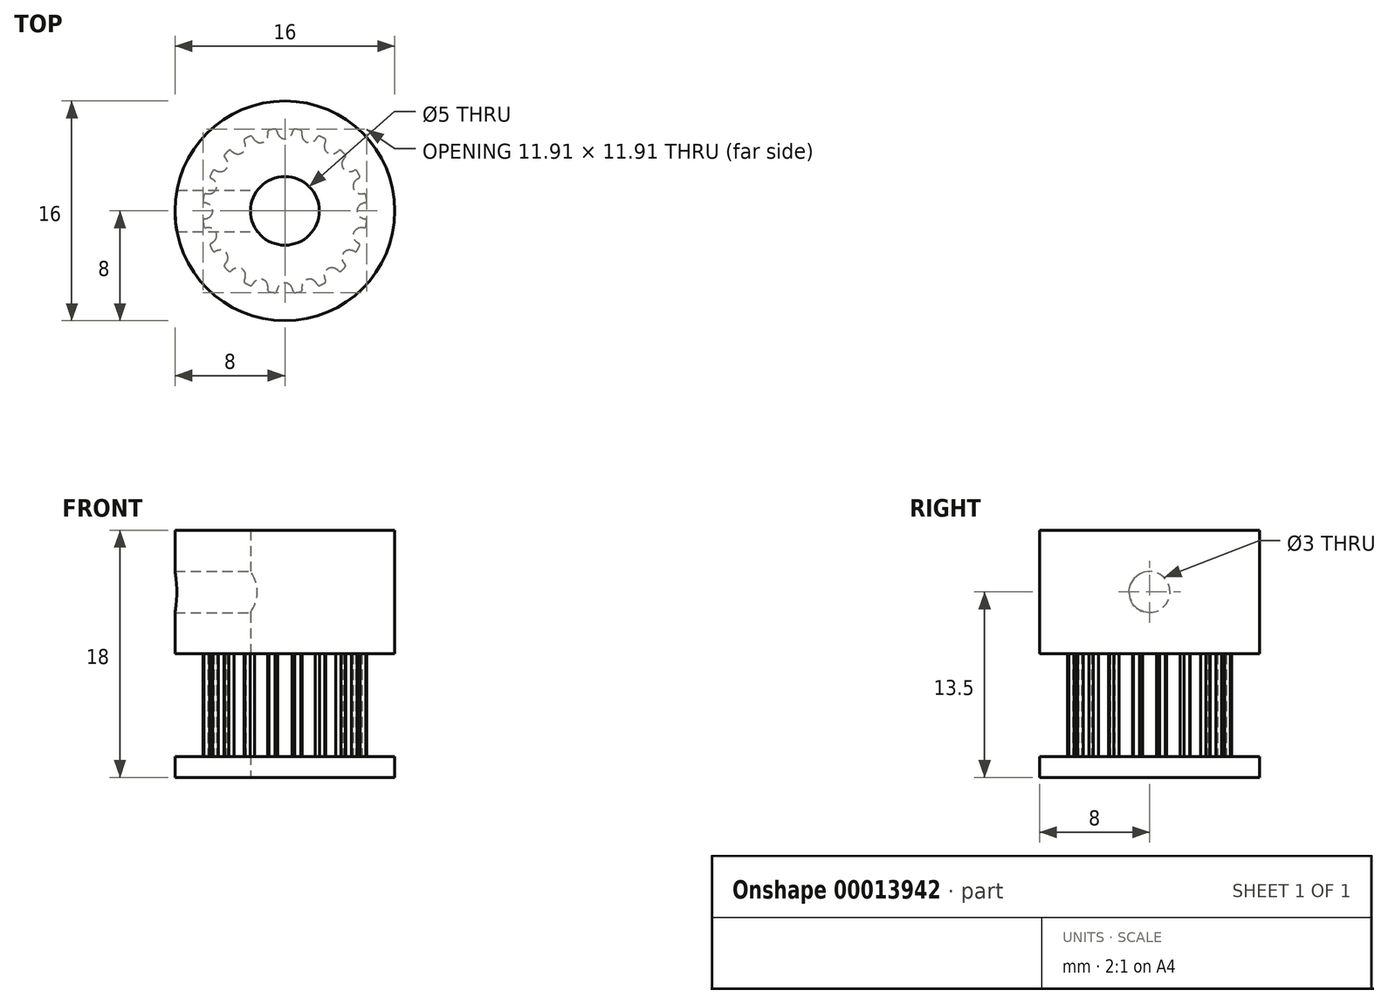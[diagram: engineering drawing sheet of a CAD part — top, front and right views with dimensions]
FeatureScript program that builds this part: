
annotation { "Feature Type Name" : "Feature", "Feature Type Description" : "" }
export const myFeature = defineFeature(function(context is Context, id is Id, definition is map)
    precondition{}
    {
        {
            var Q0;
            Q0=qCreatedBy(makeId("Top.planeOp"),FACE);
            var sketch = newSketch(context, id + "F0", { "sketchPlane" : qUnion([Q0])});
            skLineSegment(sketch, "E0", {"start": v(-19.17, 17.78) * mm, "end": v(-18.17, 17.78) * mm});
            skLineSegment(sketch, "E1", {"start": v(-18.17, 17.78) * mm, "end": v(-18.17, 18.4) * mm});
            skArc(sketch, "E2", {"start": v(-18.67, 18.85) * mm, "mid": v(-18.88, 19.07) * mm, "end": v(-19.17, 19.16) * mm});
            skArc(sketch, "E3", {"start": v(-18.58, 18.54) * mm, "mid": v(-18.61, 18.7) * mm, "end": v(-18.67, 18.85) * mm});
            skArc(sketch, "E4", {"start": v(-18.58, 18.54) * mm, "mid": v(-18.53, 18.44) * mm, "end": v(-18.43, 18.4) * mm});
            skLineSegment(sketch, "E5", {"start": v(-18.43, 18.4) * mm, "end": v(-18.17, 18.4) * mm});
            skArc(sketch, "E6.0.MirrorCS", {"start": v(-19.67, 18.85) * mm, "mid": v(-19.47, 19.07) * mm, "end": v(-19.17, 19.16) * mm});
            skArc(sketch, "E7.0.MirrorCS", {"start": v(-19.76, 18.54) * mm, "mid": v(-19.73, 18.7) * mm, "end": v(-19.67, 18.85) * mm});
            skArc(sketch, "E8.0.MirrorCS", {"start": v(-19.76, 18.54) * mm, "mid": v(-19.81, 18.44) * mm, "end": v(-19.91, 18.4) * mm});
            skLineSegment(sketch, "E9.0.MirrorCS", {"start": v(-19.91, 18.4) * mm, "end": v(-20.17, 18.4) * mm});
            skLineSegment(sketch, "E10.0.MirrorCS", {"start": v(-20.17, 17.78) * mm, "end": v(-20.17, 18.4) * mm});
            skLineSegment(sketch, "E11.0.MirrorCS", {"start": v(-19.17, 17.78) * mm, "end": v(-20.17, 17.78) * mm});
            skLineSegment(sketch, "E12.direction1", {"start": v(-20.17, 17.78) * mm, "end": v(-18.17, 17.78) * mm, "construction": true});
            skLineSegment(sketch, "E13", {"start": v(-20.17, 18.15) * mm, "end": v(-18.17, 18.15) * mm, "construction": true});
            skPoint(sketch, "E14", {"position": v(0, -5.25) * mm});
            skArc(sketch, "E15", {"start": v(0.51, -5.6) * mm, "mid": v(0, -5.25) * mm, "end": v(-0.51, -5.6) * mm});
            skArc(sketch, "E16", {"start": v(-0.51, -5.6) * mm, "mid": v(-0.56, -5.71) * mm, "end": v(-0.59, -5.83) * mm});
            skArc(sketch, "E17", {"start": v(0.59, -5.83) * mm, "mid": v(0.56, -5.71) * mm, "end": v(0.51, -5.6) * mm});
            skArc(sketch, "E18", {"start": v(0.72, -5.96) * mm, "mid": v(0.94, -5.93) * mm, "end": v(1.16, -5.89) * mm});
            skArc(sketch, "E19", {"start": v(0.59, -5.83) * mm, "mid": v(0.66, -5.94) * mm, "end": v(0.8, -5.95) * mm});
            skArc(sketch, "E20", {"start": v(-0.59, -5.83) * mm, "mid": v(-0.66, -5.94) * mm, "end": v(-0.8, -5.95) * mm});
            skArc(sketch, "E21.1.0", {"start": v(2.22, -5.16) * mm, "mid": v(1.62, -5) * mm, "end": v(1.24, -5.48) * mm});
            skPoint(sketch, "E21.1.1", {"position": v(1.62, -5) * mm});
            skArc(sketch, "E21.1.2", {"start": v(1.24, -5.48) * mm, "mid": v(1.23, -5.6) * mm, "end": v(1.24, -5.73) * mm});
            skArc(sketch, "E21.1.3", {"start": v(2.36, -5.37) * mm, "mid": v(2.47, -5.44) * mm, "end": v(2.6, -5.41) * mm});
            skArc(sketch, "E21.1.4", {"start": v(1.24, -5.73) * mm, "mid": v(1.2, -5.85) * mm, "end": v(1.08, -5.9) * mm});
            skArc(sketch, "E21.1.5", {"start": v(2.36, -5.37) * mm, "mid": v(2.3, -5.26) * mm, "end": v(2.22, -5.16) * mm});
            skArc(sketch, "E22.3.2.0", {"start": v(3.7, -4.22) * mm, "mid": v(3.09, -4.25) * mm, "end": v(2.87, -4.83) * mm});
            skPoint(sketch, "E22.4.2.0", {"position": v(3.09, -4.25) * mm});
            skArc(sketch, "E22.5.2.0", {"start": v(2.87, -4.83) * mm, "mid": v(2.9, -4.95) * mm, "end": v(2.95, -5.07) * mm});
            skArc(sketch, "E22.9.2.0", {"start": v(3.9, -4.37) * mm, "mid": v(4.03, -4.41) * mm, "end": v(4.14, -4.35) * mm});
            skArc(sketch, "E22.13.2.0", {"start": v(2.95, -5.07) * mm, "mid": v(2.95, -5.2) * mm, "end": v(2.85, -5.28) * mm});
            skArc(sketch, "E22.17.2.0", {"start": v(3.9, -4.37) * mm, "mid": v(3.81, -4.3) * mm, "end": v(3.7, -4.22) * mm});
            skArc(sketch, "E22.3.3.0", {"start": v(4.83, -2.87) * mm, "mid": v(4.25, -3.09) * mm, "end": v(4.22, -3.7) * mm});
            skPoint(sketch, "E22.4.3.0", {"position": v(4.25, -3.09) * mm});
            skArc(sketch, "E22.5.3.0", {"start": v(4.22, -3.7) * mm, "mid": v(4.3, -3.81) * mm, "end": v(4.37, -3.9) * mm});
            skArc(sketch, "E22.9.3.0", {"start": v(5.07, -2.95) * mm, "mid": v(5.2, -2.95) * mm, "end": v(5.28, -2.85) * mm});
            skArc(sketch, "E22.13.3.0", {"start": v(4.37, -3.9) * mm, "mid": v(4.41, -4.03) * mm, "end": v(4.35, -4.14) * mm});
            skArc(sketch, "E22.17.3.0", {"start": v(5.07, -2.95) * mm, "mid": v(4.95, -2.9) * mm, "end": v(4.83, -2.87) * mm});
            skArc(sketch, "E22.3.4.0", {"start": v(5.48, -1.24) * mm, "mid": v(5, -1.62) * mm, "end": v(5.16, -2.22) * mm});
            skPoint(sketch, "E22.4.4.0", {"position": v(5, -1.62) * mm});
            skArc(sketch, "E22.5.4.0", {"start": v(5.16, -2.22) * mm, "mid": v(5.26, -2.3) * mm, "end": v(5.37, -2.36) * mm});
            skArc(sketch, "E22.9.4.0", {"start": v(5.73, -1.24) * mm, "mid": v(5.85, -1.2) * mm, "end": v(5.9, -1.08) * mm});
            skArc(sketch, "E22.13.4.0", {"start": v(5.37, -2.36) * mm, "mid": v(5.44, -2.47) * mm, "end": v(5.41, -2.6) * mm});
            skArc(sketch, "E22.17.4.0", {"start": v(5.73, -1.24) * mm, "mid": v(5.6, -1.23) * mm, "end": v(5.48, -1.24) * mm});
            skArc(sketch, "E22.3.5.0", {"start": v(5.6, 0.51) * mm, "mid": v(5.25, 0) * mm, "end": v(5.6, -0.51) * mm});
            skPoint(sketch, "E22.4.5.0", {"position": v(5.25, 0) * mm});
            skArc(sketch, "E22.5.5.0", {"start": v(5.6, -0.51) * mm, "mid": v(5.71, -0.56) * mm, "end": v(5.83, -0.59) * mm});
            skArc(sketch, "E22.9.5.0", {"start": v(5.83, 0.59) * mm, "mid": v(5.94, 0.66) * mm, "end": v(5.95, 0.8) * mm});
            skArc(sketch, "E22.13.5.0", {"start": v(5.83, -0.59) * mm, "mid": v(5.94, -0.66) * mm, "end": v(5.95, -0.8) * mm});
            skArc(sketch, "E22.17.5.0", {"start": v(5.83, 0.59) * mm, "mid": v(5.71, 0.56) * mm, "end": v(5.6, 0.51) * mm});
            skArc(sketch, "E22.3.6.0", {"start": v(5.16, 2.22) * mm, "mid": v(5, 1.62) * mm, "end": v(5.48, 1.24) * mm});
            skPoint(sketch, "E22.4.6.0", {"position": v(5, 1.62) * mm});
            skArc(sketch, "E22.5.6.0", {"start": v(5.48, 1.24) * mm, "mid": v(5.6, 1.23) * mm, "end": v(5.73, 1.24) * mm});
            skArc(sketch, "E22.9.6.0", {"start": v(5.37, 2.36) * mm, "mid": v(5.44, 2.47) * mm, "end": v(5.41, 2.6) * mm});
            skArc(sketch, "E22.13.6.0", {"start": v(5.73, 1.24) * mm, "mid": v(5.85, 1.2) * mm, "end": v(5.9, 1.08) * mm});
            skArc(sketch, "E22.17.6.0", {"start": v(5.37, 2.36) * mm, "mid": v(5.26, 2.3) * mm, "end": v(5.16, 2.22) * mm});
            skArc(sketch, "E22.3.7.0", {"start": v(4.22, 3.7) * mm, "mid": v(4.25, 3.09) * mm, "end": v(4.83, 2.87) * mm});
            skPoint(sketch, "E22.4.7.0", {"position": v(4.25, 3.09) * mm});
            skArc(sketch, "E22.5.7.0", {"start": v(4.83, 2.87) * mm, "mid": v(4.95, 2.9) * mm, "end": v(5.07, 2.95) * mm});
            skArc(sketch, "E22.9.7.0", {"start": v(4.37, 3.9) * mm, "mid": v(4.41, 4.03) * mm, "end": v(4.35, 4.14) * mm});
            skArc(sketch, "E22.13.7.0", {"start": v(5.07, 2.95) * mm, "mid": v(5.2, 2.95) * mm, "end": v(5.28, 2.85) * mm});
            skArc(sketch, "E22.17.7.0", {"start": v(4.37, 3.9) * mm, "mid": v(4.3, 3.81) * mm, "end": v(4.22, 3.7) * mm});
            skArc(sketch, "E22.3.8.0", {"start": v(2.87, 4.83) * mm, "mid": v(3.09, 4.25) * mm, "end": v(3.7, 4.22) * mm});
            skPoint(sketch, "E22.4.8.0", {"position": v(3.09, 4.25) * mm});
            skArc(sketch, "E22.5.8.0", {"start": v(3.7, 4.22) * mm, "mid": v(3.81, 4.3) * mm, "end": v(3.9, 4.37) * mm});
            skArc(sketch, "E22.9.8.0", {"start": v(2.95, 5.07) * mm, "mid": v(2.95, 5.2) * mm, "end": v(2.85, 5.28) * mm});
            skArc(sketch, "E22.13.8.0", {"start": v(3.9, 4.37) * mm, "mid": v(4.03, 4.41) * mm, "end": v(4.14, 4.35) * mm});
            skArc(sketch, "E22.17.8.0", {"start": v(2.95, 5.07) * mm, "mid": v(2.9, 4.95) * mm, "end": v(2.87, 4.83) * mm});
            skArc(sketch, "E22.3.9.0", {"start": v(1.24, 5.48) * mm, "mid": v(1.62, 5) * mm, "end": v(2.22, 5.16) * mm});
            skPoint(sketch, "E22.4.9.0", {"position": v(1.62, 5) * mm});
            skArc(sketch, "E22.5.9.0", {"start": v(2.22, 5.16) * mm, "mid": v(2.3, 5.26) * mm, "end": v(2.36, 5.37) * mm});
            skArc(sketch, "E22.9.9.0", {"start": v(1.24, 5.73) * mm, "mid": v(1.2, 5.85) * mm, "end": v(1.08, 5.9) * mm});
            skArc(sketch, "E22.13.9.0", {"start": v(2.36, 5.37) * mm, "mid": v(2.47, 5.44) * mm, "end": v(2.6, 5.41) * mm});
            skArc(sketch, "E22.17.9.0", {"start": v(1.24, 5.73) * mm, "mid": v(1.23, 5.6) * mm, "end": v(1.24, 5.48) * mm});
            skArc(sketch, "E22.3.10.0", {"start": v(-0.51, 5.6) * mm, "mid": v(0, 5.25) * mm, "end": v(0.51, 5.6) * mm});
            skPoint(sketch, "E22.4.10.0", {"position": v(0, 5.25) * mm});
            skArc(sketch, "E22.5.10.0", {"start": v(0.51, 5.6) * mm, "mid": v(0.56, 5.71) * mm, "end": v(0.59, 5.83) * mm});
            skArc(sketch, "E22.9.10.0", {"start": v(-0.59, 5.83) * mm, "mid": v(-0.66, 5.94) * mm, "end": v(-0.8, 5.95) * mm});
            skArc(sketch, "E22.13.10.0", {"start": v(0.59, 5.83) * mm, "mid": v(0.66, 5.94) * mm, "end": v(0.8, 5.95) * mm});
            skArc(sketch, "E22.17.10.0", {"start": v(-0.59, 5.83) * mm, "mid": v(-0.56, 5.71) * mm, "end": v(-0.51, 5.6) * mm});
            skArc(sketch, "E22.3.11.0", {"start": v(-2.22, 5.16) * mm, "mid": v(-1.62, 5) * mm, "end": v(-1.24, 5.48) * mm});
            skPoint(sketch, "E22.4.11.0", {"position": v(-1.62, 5) * mm});
            skArc(sketch, "E22.5.11.0", {"start": v(-1.24, 5.48) * mm, "mid": v(-1.23, 5.6) * mm, "end": v(-1.24, 5.73) * mm});
            skArc(sketch, "E22.9.11.0", {"start": v(-2.36, 5.37) * mm, "mid": v(-2.47, 5.44) * mm, "end": v(-2.6, 5.41) * mm});
            skArc(sketch, "E22.13.11.0", {"start": v(-1.24, 5.73) * mm, "mid": v(-1.2, 5.85) * mm, "end": v(-1.08, 5.9) * mm});
            skArc(sketch, "E22.17.11.0", {"start": v(-2.36, 5.37) * mm, "mid": v(-2.3, 5.26) * mm, "end": v(-2.22, 5.16) * mm});
            skArc(sketch, "E22.3.12.0", {"start": v(-3.7, 4.22) * mm, "mid": v(-3.09, 4.25) * mm, "end": v(-2.87, 4.83) * mm});
            skPoint(sketch, "E22.4.12.0", {"position": v(-3.09, 4.25) * mm});
            skArc(sketch, "E22.5.12.0", {"start": v(-2.87, 4.83) * mm, "mid": v(-2.9, 4.95) * mm, "end": v(-2.95, 5.07) * mm});
            skArc(sketch, "E22.9.12.0", {"start": v(-3.9, 4.37) * mm, "mid": v(-4.03, 4.41) * mm, "end": v(-4.14, 4.35) * mm});
            skArc(sketch, "E22.13.12.0", {"start": v(-2.95, 5.07) * mm, "mid": v(-2.95, 5.2) * mm, "end": v(-2.85, 5.28) * mm});
            skArc(sketch, "E22.17.12.0", {"start": v(-3.9, 4.37) * mm, "mid": v(-3.81, 4.3) * mm, "end": v(-3.7, 4.22) * mm});
            skArc(sketch, "E22.3.13.0", {"start": v(-4.83, 2.87) * mm, "mid": v(-4.25, 3.09) * mm, "end": v(-4.22, 3.7) * mm});
            skPoint(sketch, "E22.4.13.0", {"position": v(-4.25, 3.09) * mm});
            skArc(sketch, "E22.5.13.0", {"start": v(-4.22, 3.7) * mm, "mid": v(-4.3, 3.81) * mm, "end": v(-4.37, 3.9) * mm});
            skArc(sketch, "E22.9.13.0", {"start": v(-5.07, 2.95) * mm, "mid": v(-5.2, 2.95) * mm, "end": v(-5.28, 2.85) * mm});
            skArc(sketch, "E22.13.13.0", {"start": v(-4.37, 3.9) * mm, "mid": v(-4.41, 4.03) * mm, "end": v(-4.35, 4.14) * mm});
            skArc(sketch, "E22.17.13.0", {"start": v(-5.07, 2.95) * mm, "mid": v(-4.95, 2.9) * mm, "end": v(-4.83, 2.87) * mm});
            skArc(sketch, "E22.3.14.0", {"start": v(-5.48, 1.24) * mm, "mid": v(-5, 1.62) * mm, "end": v(-5.16, 2.22) * mm});
            skPoint(sketch, "E22.4.14.0", {"position": v(-5, 1.62) * mm});
            skArc(sketch, "E22.5.14.0", {"start": v(-5.16, 2.22) * mm, "mid": v(-5.26, 2.3) * mm, "end": v(-5.37, 2.36) * mm});
            skArc(sketch, "E22.9.14.0", {"start": v(-5.73, 1.24) * mm, "mid": v(-5.85, 1.2) * mm, "end": v(-5.9, 1.08) * mm});
            skArc(sketch, "E22.13.14.0", {"start": v(-5.37, 2.36) * mm, "mid": v(-5.44, 2.47) * mm, "end": v(-5.41, 2.6) * mm});
            skArc(sketch, "E22.17.14.0", {"start": v(-5.73, 1.24) * mm, "mid": v(-5.6, 1.23) * mm, "end": v(-5.48, 1.24) * mm});
            skArc(sketch, "E22.3.15.0", {"start": v(-5.6, -0.51) * mm, "mid": v(-5.25, 0) * mm, "end": v(-5.6, 0.51) * mm});
            skPoint(sketch, "E22.4.15.0", {"position": v(-5.25, 0) * mm});
            skArc(sketch, "E22.5.15.0", {"start": v(-5.6, 0.51) * mm, "mid": v(-5.71, 0.56) * mm, "end": v(-5.83, 0.59) * mm});
            skArc(sketch, "E22.9.15.0", {"start": v(-5.83, -0.59) * mm, "mid": v(-5.94, -0.66) * mm, "end": v(-5.95, -0.8) * mm});
            skArc(sketch, "E22.13.15.0", {"start": v(-5.83, 0.59) * mm, "mid": v(-5.94, 0.66) * mm, "end": v(-5.95, 0.8) * mm});
            skArc(sketch, "E22.17.15.0", {"start": v(-5.83, -0.59) * mm, "mid": v(-5.71, -0.56) * mm, "end": v(-5.6, -0.51) * mm});
            skArc(sketch, "E22.3.16.0", {"start": v(-5.16, -2.22) * mm, "mid": v(-5, -1.62) * mm, "end": v(-5.48, -1.24) * mm});
            skPoint(sketch, "E22.4.16.0", {"position": v(-5, -1.62) * mm});
            skArc(sketch, "E22.5.16.0", {"start": v(-5.48, -1.24) * mm, "mid": v(-5.6, -1.23) * mm, "end": v(-5.73, -1.24) * mm});
            skArc(sketch, "E22.9.16.0", {"start": v(-5.37, -2.36) * mm, "mid": v(-5.44, -2.47) * mm, "end": v(-5.41, -2.6) * mm});
            skArc(sketch, "E22.13.16.0", {"start": v(-5.73, -1.24) * mm, "mid": v(-5.85, -1.2) * mm, "end": v(-5.9, -1.08) * mm});
            skArc(sketch, "E22.17.16.0", {"start": v(-5.37, -2.36) * mm, "mid": v(-5.26, -2.3) * mm, "end": v(-5.16, -2.22) * mm});
            skArc(sketch, "E22.3.17.0", {"start": v(-4.22, -3.7) * mm, "mid": v(-4.25, -3.09) * mm, "end": v(-4.83, -2.87) * mm});
            skPoint(sketch, "E22.4.17.0", {"position": v(-4.25, -3.09) * mm});
            skArc(sketch, "E22.5.17.0", {"start": v(-4.83, -2.87) * mm, "mid": v(-4.95, -2.9) * mm, "end": v(-5.07, -2.95) * mm});
            skArc(sketch, "E22.9.17.0", {"start": v(-4.37, -3.9) * mm, "mid": v(-4.41, -4.03) * mm, "end": v(-4.35, -4.14) * mm});
            skArc(sketch, "E22.13.17.0", {"start": v(-5.07, -2.95) * mm, "mid": v(-5.2, -2.95) * mm, "end": v(-5.28, -2.85) * mm});
            skArc(sketch, "E22.17.17.0", {"start": v(-4.37, -3.9) * mm, "mid": v(-4.3, -3.81) * mm, "end": v(-4.22, -3.7) * mm});
            skArc(sketch, "E22.3.18.0", {"start": v(-2.87, -4.83) * mm, "mid": v(-3.09, -4.25) * mm, "end": v(-3.7, -4.22) * mm});
            skPoint(sketch, "E22.4.18.0", {"position": v(-3.09, -4.25) * mm});
            skArc(sketch, "E22.5.18.0", {"start": v(-3.7, -4.22) * mm, "mid": v(-3.81, -4.3) * mm, "end": v(-3.9, -4.37) * mm});
            skArc(sketch, "E22.9.18.0", {"start": v(-2.95, -5.07) * mm, "mid": v(-2.95, -5.2) * mm, "end": v(-2.85, -5.28) * mm});
            skArc(sketch, "E22.13.18.0", {"start": v(-3.9, -4.37) * mm, "mid": v(-4.03, -4.41) * mm, "end": v(-4.14, -4.35) * mm});
            skArc(sketch, "E22.17.18.0", {"start": v(-2.95, -5.07) * mm, "mid": v(-2.9, -4.95) * mm, "end": v(-2.87, -4.83) * mm});
            skArc(sketch, "E22.3.19.0", {"start": v(-1.24, -5.48) * mm, "mid": v(-1.62, -5) * mm, "end": v(-2.22, -5.16) * mm});
            skPoint(sketch, "E22.4.19.0", {"position": v(-1.62, -5) * mm});
            skArc(sketch, "E22.5.19.0", {"start": v(-2.22, -5.16) * mm, "mid": v(-2.3, -5.26) * mm, "end": v(-2.36, -5.37) * mm});
            skArc(sketch, "E22.9.19.0", {"start": v(-1.24, -5.73) * mm, "mid": v(-1.2, -5.85) * mm, "end": v(-1.08, -5.9) * mm});
            skArc(sketch, "E22.13.19.0", {"start": v(-2.36, -5.37) * mm, "mid": v(-2.47, -5.44) * mm, "end": v(-2.6, -5.41) * mm});
            skArc(sketch, "E22.17.19.0", {"start": v(-1.24, -5.73) * mm, "mid": v(-1.23, -5.6) * mm, "end": v(-1.24, -5.48) * mm});
            skArc(sketch, "E23.trimOffspring", {"start": v(2.52, -5.44) * mm, "mid": v(2.72, -5.35) * mm, "end": v(2.92, -5.24) * mm});
            skArc(sketch, "E24.trimOffspring", {"start": v(4.08, -4.4) * mm, "mid": v(4.24, -4.24) * mm, "end": v(4.4, -4.08) * mm});
            skArc(sketch, "E25.trimOffspring", {"start": v(5.24, -2.92) * mm, "mid": v(5.33, -2.76) * mm, "end": v(5.41, -2.6) * mm});
            skArc(sketch, "E26.trimOffspring", {"start": v(5.89, -1.16) * mm, "mid": v(5.93, -0.94) * mm, "end": v(5.96, -0.72) * mm});
            skArc(sketch, "E27.trimOffspring", {"start": v(5.44, 2.52) * mm, "mid": v(5.35, 2.72) * mm, "end": v(5.24, 2.92) * mm});
            skArc(sketch, "E28.trimOffspring", {"start": v(4.4, 4.08) * mm, "mid": v(4.24, 4.24) * mm, "end": v(4.08, 4.4) * mm});
            skArc(sketch, "E29.trimOffspring", {"start": v(5.96, 0.72) * mm, "mid": v(5.93, 0.94) * mm, "end": v(5.89, 1.16) * mm});
            skArc(sketch, "E30.trimOffspring", {"start": v(2.92, 5.24) * mm, "mid": v(2.72, 5.35) * mm, "end": v(2.52, 5.44) * mm});
            skArc(sketch, "E31.trimOffspring", {"start": v(1.16, 5.89) * mm, "mid": v(0.94, 5.93) * mm, "end": v(0.72, 5.96) * mm});
            skArc(sketch, "E32.trimOffspring", {"start": v(-0.72, 5.96) * mm, "mid": v(-0.94, 5.93) * mm, "end": v(-1.16, 5.89) * mm});
            skArc(sketch, "E33.trimOffspring", {"start": v(-2.52, 5.44) * mm, "mid": v(-2.72, 5.35) * mm, "end": v(-2.92, 5.24) * mm});
            skArc(sketch, "E34.trimOffspring", {"start": v(-4.08, 4.4) * mm, "mid": v(-4.24, 4.24) * mm, "end": v(-4.4, 4.08) * mm});
            skArc(sketch, "E35.trimOffspring", {"start": v(-5.24, 2.92) * mm, "mid": v(-5.35, 2.72) * mm, "end": v(-5.44, 2.52) * mm});
            skArc(sketch, "E36.trimOffspring", {"start": v(-5.89, 1.16) * mm, "mid": v(-5.93, 0.94) * mm, "end": v(-5.96, 0.72) * mm});
            skArc(sketch, "E37.trimOffspring", {"start": v(-5.96, -0.72) * mm, "mid": v(-5.93, -0.94) * mm, "end": v(-5.89, -1.16) * mm});
            skArc(sketch, "E38.trimOffspring", {"start": v(-5.44, -2.52) * mm, "mid": v(-5.35, -2.72) * mm, "end": v(-5.24, -2.92) * mm});
            skArc(sketch, "E39.trimOffspring", {"start": v(-4.4, -4.08) * mm, "mid": v(-4.24, -4.24) * mm, "end": v(-4.08, -4.4) * mm});
            skArc(sketch, "E40.trimOffspring", {"start": v(-2.92, -5.24) * mm, "mid": v(-2.72, -5.35) * mm, "end": v(-2.52, -5.44) * mm});
            skArc(sketch, "E41.trimOffspring", {"start": v(-1.16, -5.89) * mm, "mid": v(-0.94, -5.93) * mm, "end": v(-0.72, -5.96) * mm});
            skSolve(sketch);
        }
        {
            var Q0;
            Q0=makeQuery(id+"F0.imprint","IMPRINT",FACE,{"disambiguationData":[TD([[makeQuery(id+"F0.imprint","IMPRINT",EDGE,{"derivedFrom":sQuery(id+"F0.wireOp",EDGE,"E15")}),-1.0]])]});
            extrude(context, id + "F1", {"entities" : qUnion([Q0]), "depth" : 7.5 * mm});
        }
        {
            var Q0;
            Q0=makeQuery(id+"F1.opExtrude","CAP_FACE",FACE,{"disambiguationData":[OSD([sQuery(id+"F0.wireOp",EDGE,"E15"),sQuery(id+"F0.wireOp",EDGE,"E16"),sQuery(id+"F0.wireOp",EDGE,"E17"),sQuery(id+"F0.wireOp",EDGE,"E18"),sQuery(id+"F0.wireOp",EDGE,"E19"),sQuery(id+"F0.wireOp",EDGE,"E20"),sQuery(id+"F0.wireOp",EDGE,"E21.1.0"),sQuery(id+"F0.wireOp",EDGE,"E21.1.2"),sQuery(id+"F0.wireOp",EDGE,"E21.1.3"),sQuery(id+"F0.wireOp",EDGE,"E21.1.4"),sQuery(id+"F0.wireOp",EDGE,"E21.1.5"),sQuery(id+"F0.wireOp",EDGE,"E22.3.2.0"),sQuery(id+"F0.wireOp",EDGE,"E22.5.2.0"),sQuery(id+"F0.wireOp",EDGE,"E22.9.2.0"),sQuery(id+"F0.wireOp",EDGE,"E22.13.2.0"),sQuery(id+"F0.wireOp",EDGE,"E22.17.2.0"),sQuery(id+"F0.wireOp",EDGE,"E22.3.3.0"),sQuery(id+"F0.wireOp",EDGE,"E22.5.3.0"),sQuery(id+"F0.wireOp",EDGE,"E22.9.3.0"),sQuery(id+"F0.wireOp",EDGE,"E22.13.3.0"),sQuery(id+"F0.wireOp",EDGE,"E22.17.3.0"),sQuery(id+"F0.wireOp",EDGE,"E22.3.4.0"),sQuery(id+"F0.wireOp",EDGE,"E22.5.4.0"),sQuery(id+"F0.wireOp",EDGE,"E22.9.4.0"),sQuery(id+"F0.wireOp",EDGE,"E22.13.4.0"),sQuery(id+"F0.wireOp",EDGE,"E22.17.4.0"),sQuery(id+"F0.wireOp",EDGE,"E22.3.5.0"),sQuery(id+"F0.wireOp",EDGE,"E22.5.5.0"),sQuery(id+"F0.wireOp",EDGE,"E22.9.5.0"),sQuery(id+"F0.wireOp",EDGE,"E22.13.5.0"),sQuery(id+"F0.wireOp",EDGE,"E22.17.5.0"),sQuery(id+"F0.wireOp",EDGE,"E22.3.6.0"),sQuery(id+"F0.wireOp",EDGE,"E22.5.6.0"),sQuery(id+"F0.wireOp",EDGE,"E22.9.6.0"),sQuery(id+"F0.wireOp",EDGE,"E22.13.6.0"),sQuery(id+"F0.wireOp",EDGE,"E22.17.6.0"),sQuery(id+"F0.wireOp",EDGE,"E22.3.7.0"),sQuery(id+"F0.wireOp",EDGE,"E22.5.7.0"),sQuery(id+"F0.wireOp",EDGE,"E22.9.7.0"),sQuery(id+"F0.wireOp",EDGE,"E22.13.7.0"),sQuery(id+"F0.wireOp",EDGE,"E22.17.7.0"),sQuery(id+"F0.wireOp",EDGE,"E22.3.8.0"),sQuery(id+"F0.wireOp",EDGE,"E22.5.8.0"),sQuery(id+"F0.wireOp",EDGE,"E22.9.8.0"),sQuery(id+"F0.wireOp",EDGE,"E22.13.8.0"),sQuery(id+"F0.wireOp",EDGE,"E22.17.8.0"),sQuery(id+"F0.wireOp",EDGE,"E22.3.9.0"),sQuery(id+"F0.wireOp",EDGE,"E22.5.9.0"),sQuery(id+"F0.wireOp",EDGE,"E22.9.9.0"),sQuery(id+"F0.wireOp",EDGE,"E22.13.9.0"),sQuery(id+"F0.wireOp",EDGE,"E22.17.9.0"),sQuery(id+"F0.wireOp",EDGE,"E22.3.10.0"),sQuery(id+"F0.wireOp",EDGE,"E22.5.10.0"),sQuery(id+"F0.wireOp",EDGE,"E22.9.10.0"),sQuery(id+"F0.wireOp",EDGE,"E22.13.10.0"),sQuery(id+"F0.wireOp",EDGE,"E22.17.10.0"),sQuery(id+"F0.wireOp",EDGE,"E22.3.11.0"),sQuery(id+"F0.wireOp",EDGE,"E22.5.11.0"),sQuery(id+"F0.wireOp",EDGE,"E22.9.11.0"),sQuery(id+"F0.wireOp",EDGE,"E22.13.11.0"),sQuery(id+"F0.wireOp",EDGE,"E22.17.11.0"),sQuery(id+"F0.wireOp",EDGE,"E22.3.12.0"),sQuery(id+"F0.wireOp",EDGE,"E22.5.12.0"),sQuery(id+"F0.wireOp",EDGE,"E22.9.12.0"),sQuery(id+"F0.wireOp",EDGE,"E22.13.12.0"),sQuery(id+"F0.wireOp",EDGE,"E22.17.12.0"),sQuery(id+"F0.wireOp",EDGE,"E22.3.13.0"),sQuery(id+"F0.wireOp",EDGE,"E22.5.13.0"),sQuery(id+"F0.wireOp",EDGE,"E22.9.13.0"),sQuery(id+"F0.wireOp",EDGE,"E22.13.13.0"),sQuery(id+"F0.wireOp",EDGE,"E22.17.13.0"),sQuery(id+"F0.wireOp",EDGE,"E22.3.14.0"),sQuery(id+"F0.wireOp",EDGE,"E22.5.14.0"),sQuery(id+"F0.wireOp",EDGE,"E22.9.14.0"),sQuery(id+"F0.wireOp",EDGE,"E22.13.14.0"),sQuery(id+"F0.wireOp",EDGE,"E22.17.14.0"),sQuery(id+"F0.wireOp",EDGE,"E22.3.15.0"),sQuery(id+"F0.wireOp",EDGE,"E22.5.15.0"),sQuery(id+"F0.wireOp",EDGE,"E22.9.15.0"),sQuery(id+"F0.wireOp",EDGE,"E22.13.15.0"),sQuery(id+"F0.wireOp",EDGE,"E22.17.15.0"),sQuery(id+"F0.wireOp",EDGE,"E22.3.16.0"),sQuery(id+"F0.wireOp",EDGE,"E22.5.16.0"),sQuery(id+"F0.wireOp",EDGE,"E22.9.16.0"),sQuery(id+"F0.wireOp",EDGE,"E22.13.16.0"),sQuery(id+"F0.wireOp",EDGE,"E22.17.16.0"),sQuery(id+"F0.wireOp",EDGE,"E22.3.17.0"),sQuery(id+"F0.wireOp",EDGE,"E22.5.17.0"),sQuery(id+"F0.wireOp",EDGE,"E22.9.17.0"),sQuery(id+"F0.wireOp",EDGE,"E22.13.17.0"),sQuery(id+"F0.wireOp",EDGE,"E22.17.17.0"),sQuery(id+"F0.wireOp",EDGE,"E22.3.18.0"),sQuery(id+"F0.wireOp",EDGE,"E22.5.18.0"),sQuery(id+"F0.wireOp",EDGE,"E22.9.18.0"),sQuery(id+"F0.wireOp",EDGE,"E22.13.18.0"),sQuery(id+"F0.wireOp",EDGE,"E22.17.18.0"),sQuery(id+"F0.wireOp",EDGE,"E22.3.19.0"),sQuery(id+"F0.wireOp",EDGE,"E22.5.19.0"),sQuery(id+"F0.wireOp",EDGE,"E22.9.19.0"),sQuery(id+"F0.wireOp",EDGE,"E22.13.19.0"),sQuery(id+"F0.wireOp",EDGE,"E22.17.19.0"),sQuery(id+"F0.wireOp",EDGE,"E23.trimOffspring"),sQuery(id+"F0.wireOp",EDGE,"E24.trimOffspring"),sQuery(id+"F0.wireOp",EDGE,"E25.trimOffspring"),sQuery(id+"F0.wireOp",EDGE,"E26.trimOffspring"),sQuery(id+"F0.wireOp",EDGE,"E27.trimOffspring"),sQuery(id+"F0.wireOp",EDGE,"E28.trimOffspring"),sQuery(id+"F0.wireOp",EDGE,"E29.trimOffspring"),sQuery(id+"F0.wireOp",EDGE,"E30.trimOffspring"),sQuery(id+"F0.wireOp",EDGE,"E31.trimOffspring"),sQuery(id+"F0.wireOp",EDGE,"E32.trimOffspring"),sQuery(id+"F0.wireOp",EDGE,"E33.trimOffspring"),sQuery(id+"F0.wireOp",EDGE,"E34.trimOffspring"),sQuery(id+"F0.wireOp",EDGE,"E35.trimOffspring"),sQuery(id+"F0.wireOp",EDGE,"E36.trimOffspring"),sQuery(id+"F0.wireOp",EDGE,"E37.trimOffspring"),sQuery(id+"F0.wireOp",EDGE,"E38.trimOffspring"),sQuery(id+"F0.wireOp",EDGE,"E39.trimOffspring"),sQuery(id+"F0.wireOp",EDGE,"E40.trimOffspring"),sQuery(id+"F0.wireOp",EDGE,"E41.trimOffspring")])],"isStart":false});
            var sketch = newSketch(context, id + "F2", { "sketchPlane" : qUnion([Q0])});
            skCircle(sketch, "E42", {"center": v(0, 0) * mm, "radius": 8 * mm});
            skSolve(sketch);
        }
        {
            var Q0;
            Q0 = qSketchRegion(id + "F2", true);
            extrude(context, id + "F3", {"entities" : qUnion([Q0]), "operationType" : NewBodyOperationType.ADD, "depth" : 9 * mm});
        }
        {
            var Q0;
            Q0=makeQuery(id+"F1.opExtrude","CAP_FACE",FACE,{"disambiguationData":[OSD([sQuery(id+"F0.wireOp",EDGE,"E15"),sQuery(id+"F0.wireOp",EDGE,"E16"),sQuery(id+"F0.wireOp",EDGE,"E17"),sQuery(id+"F0.wireOp",EDGE,"E18"),sQuery(id+"F0.wireOp",EDGE,"E19"),sQuery(id+"F0.wireOp",EDGE,"E20"),sQuery(id+"F0.wireOp",EDGE,"E21.1.0"),sQuery(id+"F0.wireOp",EDGE,"E21.1.2"),sQuery(id+"F0.wireOp",EDGE,"E21.1.3"),sQuery(id+"F0.wireOp",EDGE,"E21.1.4"),sQuery(id+"F0.wireOp",EDGE,"E21.1.5"),sQuery(id+"F0.wireOp",EDGE,"E22.3.2.0"),sQuery(id+"F0.wireOp",EDGE,"E22.5.2.0"),sQuery(id+"F0.wireOp",EDGE,"E22.9.2.0"),sQuery(id+"F0.wireOp",EDGE,"E22.13.2.0"),sQuery(id+"F0.wireOp",EDGE,"E22.17.2.0"),sQuery(id+"F0.wireOp",EDGE,"E22.3.3.0"),sQuery(id+"F0.wireOp",EDGE,"E22.5.3.0"),sQuery(id+"F0.wireOp",EDGE,"E22.9.3.0"),sQuery(id+"F0.wireOp",EDGE,"E22.13.3.0"),sQuery(id+"F0.wireOp",EDGE,"E22.17.3.0"),sQuery(id+"F0.wireOp",EDGE,"E22.3.4.0"),sQuery(id+"F0.wireOp",EDGE,"E22.5.4.0"),sQuery(id+"F0.wireOp",EDGE,"E22.9.4.0"),sQuery(id+"F0.wireOp",EDGE,"E22.13.4.0"),sQuery(id+"F0.wireOp",EDGE,"E22.17.4.0"),sQuery(id+"F0.wireOp",EDGE,"E22.3.5.0"),sQuery(id+"F0.wireOp",EDGE,"E22.5.5.0"),sQuery(id+"F0.wireOp",EDGE,"E22.9.5.0"),sQuery(id+"F0.wireOp",EDGE,"E22.13.5.0"),sQuery(id+"F0.wireOp",EDGE,"E22.17.5.0"),sQuery(id+"F0.wireOp",EDGE,"E22.3.6.0"),sQuery(id+"F0.wireOp",EDGE,"E22.5.6.0"),sQuery(id+"F0.wireOp",EDGE,"E22.9.6.0"),sQuery(id+"F0.wireOp",EDGE,"E22.13.6.0"),sQuery(id+"F0.wireOp",EDGE,"E22.17.6.0"),sQuery(id+"F0.wireOp",EDGE,"E22.3.7.0"),sQuery(id+"F0.wireOp",EDGE,"E22.5.7.0"),sQuery(id+"F0.wireOp",EDGE,"E22.9.7.0"),sQuery(id+"F0.wireOp",EDGE,"E22.13.7.0"),sQuery(id+"F0.wireOp",EDGE,"E22.17.7.0"),sQuery(id+"F0.wireOp",EDGE,"E22.3.8.0"),sQuery(id+"F0.wireOp",EDGE,"E22.5.8.0"),sQuery(id+"F0.wireOp",EDGE,"E22.9.8.0"),sQuery(id+"F0.wireOp",EDGE,"E22.13.8.0"),sQuery(id+"F0.wireOp",EDGE,"E22.17.8.0"),sQuery(id+"F0.wireOp",EDGE,"E22.3.9.0"),sQuery(id+"F0.wireOp",EDGE,"E22.5.9.0"),sQuery(id+"F0.wireOp",EDGE,"E22.9.9.0"),sQuery(id+"F0.wireOp",EDGE,"E22.13.9.0"),sQuery(id+"F0.wireOp",EDGE,"E22.17.9.0"),sQuery(id+"F0.wireOp",EDGE,"E22.3.10.0"),sQuery(id+"F0.wireOp",EDGE,"E22.5.10.0"),sQuery(id+"F0.wireOp",EDGE,"E22.9.10.0"),sQuery(id+"F0.wireOp",EDGE,"E22.13.10.0"),sQuery(id+"F0.wireOp",EDGE,"E22.17.10.0"),sQuery(id+"F0.wireOp",EDGE,"E22.3.11.0"),sQuery(id+"F0.wireOp",EDGE,"E22.5.11.0"),sQuery(id+"F0.wireOp",EDGE,"E22.9.11.0"),sQuery(id+"F0.wireOp",EDGE,"E22.13.11.0"),sQuery(id+"F0.wireOp",EDGE,"E22.17.11.0"),sQuery(id+"F0.wireOp",EDGE,"E22.3.12.0"),sQuery(id+"F0.wireOp",EDGE,"E22.5.12.0"),sQuery(id+"F0.wireOp",EDGE,"E22.9.12.0"),sQuery(id+"F0.wireOp",EDGE,"E22.13.12.0"),sQuery(id+"F0.wireOp",EDGE,"E22.17.12.0"),sQuery(id+"F0.wireOp",EDGE,"E22.3.13.0"),sQuery(id+"F0.wireOp",EDGE,"E22.5.13.0"),sQuery(id+"F0.wireOp",EDGE,"E22.9.13.0"),sQuery(id+"F0.wireOp",EDGE,"E22.13.13.0"),sQuery(id+"F0.wireOp",EDGE,"E22.17.13.0"),sQuery(id+"F0.wireOp",EDGE,"E22.3.14.0"),sQuery(id+"F0.wireOp",EDGE,"E22.5.14.0"),sQuery(id+"F0.wireOp",EDGE,"E22.9.14.0"),sQuery(id+"F0.wireOp",EDGE,"E22.13.14.0"),sQuery(id+"F0.wireOp",EDGE,"E22.17.14.0"),sQuery(id+"F0.wireOp",EDGE,"E22.3.15.0"),sQuery(id+"F0.wireOp",EDGE,"E22.5.15.0"),sQuery(id+"F0.wireOp",EDGE,"E22.9.15.0"),sQuery(id+"F0.wireOp",EDGE,"E22.13.15.0"),sQuery(id+"F0.wireOp",EDGE,"E22.17.15.0"),sQuery(id+"F0.wireOp",EDGE,"E22.3.16.0"),sQuery(id+"F0.wireOp",EDGE,"E22.5.16.0"),sQuery(id+"F0.wireOp",EDGE,"E22.9.16.0"),sQuery(id+"F0.wireOp",EDGE,"E22.13.16.0"),sQuery(id+"F0.wireOp",EDGE,"E22.17.16.0"),sQuery(id+"F0.wireOp",EDGE,"E22.3.17.0"),sQuery(id+"F0.wireOp",EDGE,"E22.5.17.0"),sQuery(id+"F0.wireOp",EDGE,"E22.9.17.0"),sQuery(id+"F0.wireOp",EDGE,"E22.13.17.0"),sQuery(id+"F0.wireOp",EDGE,"E22.17.17.0"),sQuery(id+"F0.wireOp",EDGE,"E22.3.18.0"),sQuery(id+"F0.wireOp",EDGE,"E22.5.18.0"),sQuery(id+"F0.wireOp",EDGE,"E22.9.18.0"),sQuery(id+"F0.wireOp",EDGE,"E22.13.18.0"),sQuery(id+"F0.wireOp",EDGE,"E22.17.18.0"),sQuery(id+"F0.wireOp",EDGE,"E22.3.19.0"),sQuery(id+"F0.wireOp",EDGE,"E22.5.19.0"),sQuery(id+"F0.wireOp",EDGE,"E22.9.19.0"),sQuery(id+"F0.wireOp",EDGE,"E22.13.19.0"),sQuery(id+"F0.wireOp",EDGE,"E22.17.19.0"),sQuery(id+"F0.wireOp",EDGE,"E23.trimOffspring"),sQuery(id+"F0.wireOp",EDGE,"E24.trimOffspring"),sQuery(id+"F0.wireOp",EDGE,"E25.trimOffspring"),sQuery(id+"F0.wireOp",EDGE,"E26.trimOffspring"),sQuery(id+"F0.wireOp",EDGE,"E27.trimOffspring"),sQuery(id+"F0.wireOp",EDGE,"E28.trimOffspring"),sQuery(id+"F0.wireOp",EDGE,"E29.trimOffspring"),sQuery(id+"F0.wireOp",EDGE,"E30.trimOffspring"),sQuery(id+"F0.wireOp",EDGE,"E31.trimOffspring"),sQuery(id+"F0.wireOp",EDGE,"E32.trimOffspring"),sQuery(id+"F0.wireOp",EDGE,"E33.trimOffspring"),sQuery(id+"F0.wireOp",EDGE,"E34.trimOffspring"),sQuery(id+"F0.wireOp",EDGE,"E35.trimOffspring"),sQuery(id+"F0.wireOp",EDGE,"E36.trimOffspring"),sQuery(id+"F0.wireOp",EDGE,"E37.trimOffspring"),sQuery(id+"F0.wireOp",EDGE,"E38.trimOffspring"),sQuery(id+"F0.wireOp",EDGE,"E39.trimOffspring"),sQuery(id+"F0.wireOp",EDGE,"E40.trimOffspring"),sQuery(id+"F0.wireOp",EDGE,"E41.trimOffspring")])],"isStart":true});
            var sketch = newSketch(context, id + "F4", { "sketchPlane" : qUnion([Q0])});
            skCircle(sketch, "E43", {"center": v(0, 0) * mm, "radius": 8 * mm});
            skSolve(sketch);
        }
        {
            var Q0;
            Q0 = qSketchRegion(id + "F4", true);
            extrude(context, id + "F5", {"entities" : qUnion([Q0]), "operationType" : NewBodyOperationType.ADD, "depth" : 1.5 * mm});
        }
        {
            var Q0;
            Q0=makeQuery(id+"F5.opExtrude","CAP_FACE",FACE,{"disambiguationData":[OSD([sQuery(id+"F4.wireOp",EDGE,"E43")])],"isStart":false});
            var sketch = newSketch(context, id + "F6", { "sketchPlane" : qUnion([Q0])});
            skCircle(sketch, "E44", {"center": v(0, 0) * mm, "radius": 2.5 * mm});
            skSolve(sketch);
        }
        {
            var Q0;
            Q0 = qSketchRegion(id + "F6", true);
            extrude(context, id + "F7", {"entities" : qUnion([Q0]), "operationType" : NewBodyOperationType.REMOVE, "endBound" : BoundingType.THROUGH_ALL, "oppositeDirection" : true, "depth" : 25 * mm});
        }
        {
            var Q0;
            Q0=qCreatedBy(makeId("Right.planeOp"),FACE);
            var sketch = newSketch(context, id + "F8", { "sketchPlane" : qUnion([Q0])});
            skCircle(sketch, "E45", {"center": v(0, 12) * mm, "radius": 1.5 * mm});
            skSolve(sketch);
        }
        {
            var Q0;
            Q0 = qSketchRegion(id + "F8", true);
            extrude(context, id + "F9", {"entities" : qUnion([Q0]), "operationType" : NewBodyOperationType.REMOVE, "endBound" : BoundingType.THROUGH_ALL, "oppositeDirection" : true, "depth" : 25 * mm});
        }
    });
